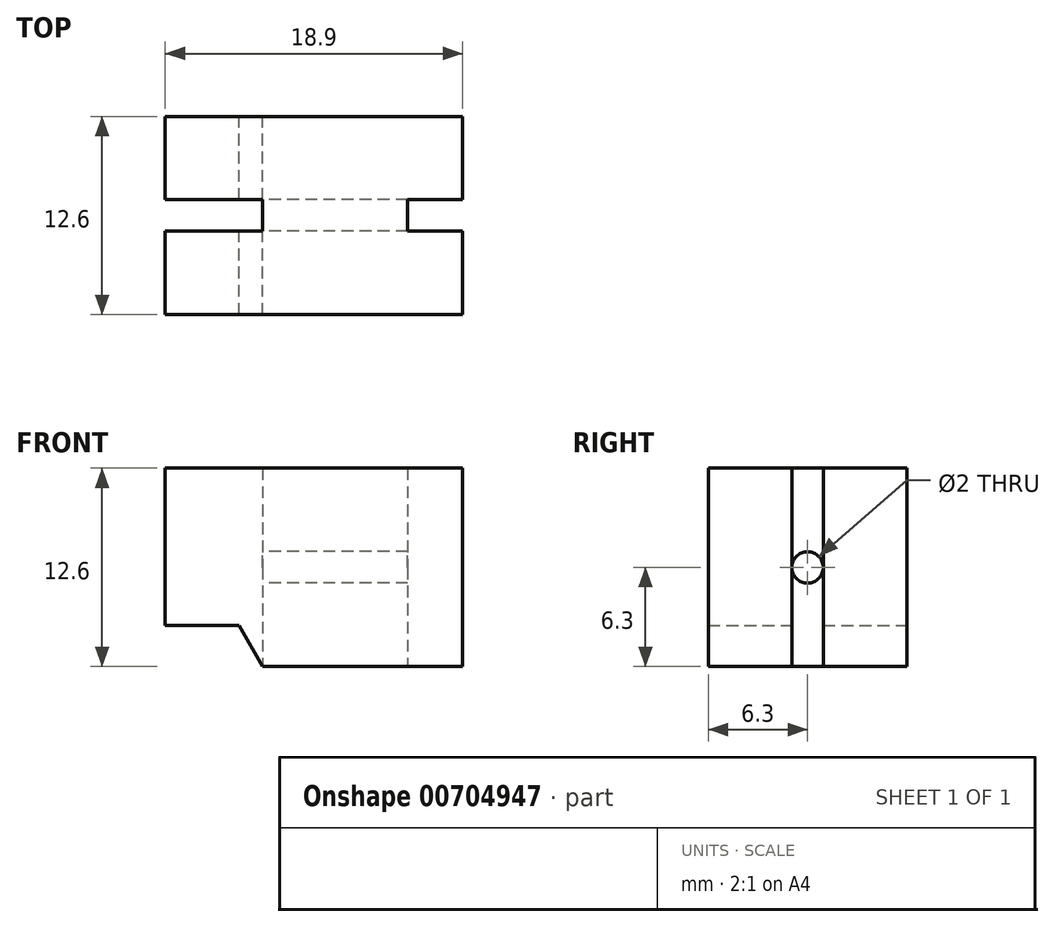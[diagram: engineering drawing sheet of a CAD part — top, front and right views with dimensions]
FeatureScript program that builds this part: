
annotation { "Feature Type Name" : "Feature", "Feature Type Description" : "" }
export const myFeature = defineFeature(function(context is Context, id is Id, definition is map)
    precondition{}
    {
        {
            var Q0;
            Q0=qCreatedBy(makeId("Front.planeOp"),FACE);
            var sketch = newSketch(context, id + "F0", { "sketchPlane" : qUnion([Q0])});
            skLineSegment(sketch, "E0", {"start": v(0, 0) * mm, "end": v(18.9, 0) * mm});
            skLineSegment(sketch, "E1", {"start": v(18.9, 0) * mm, "end": v(18.9, -12.6) * mm});
            skLineSegment(sketch, "E2", {"start": v(18.9, -12.6) * mm, "end": v(6.2, -12.6) * mm});
            skLineSegment(sketch, "E3", {"start": v(6.2, -12.6) * mm, "end": v(0, -12.6) * mm, "construction": true});
            skLineSegment(sketch, "E4", {"start": v(6.2, -12.6) * mm, "end": v(4.7, -10) * mm});
            skLineSegment(sketch, "E5", {"start": v(4.7, -10) * mm, "end": v(0, -10) * mm});
            skLineSegment(sketch, "E6", {"start": v(0, 0) * mm, "end": v(0, -10) * mm});
            skLineSegment(sketch, "E7", {"start": v(0, -12.6) * mm, "end": v(0, -10) * mm, "construction": true});
            skSolve(sketch);
        }
        {
            var Q0;
            Q0=makeQuery(id+"F0.imprint","IMPRINT",FACE,{"disambiguationData":[TD([[makeQuery(id+"F0.imprint","IMPRINT",EDGE,{"derivedFrom":sQuery(id+"F0.wireOp",EDGE,"E0")}),-1.0]])]});
            extrude(context, id + "F1", {"entities" : qUnion([Q0]), "depth" : 12.6 * mm, "offsetDistance" : 25 * mm});
        }
        {
            var Q0;
            Q0=makeQuery(id+"F1.opExtrude","SWEPT_FACE",FACE,{"disambiguationData":[OSD([sQuery(id+"F0.wireOp",EDGE,"E2")])]});
            var sketch = newSketch(context, id + "F2", { "sketchPlane" : qUnion([Q0])});
            skLineSegment(sketch, "E8.bottom", {"start": v(6.2, 7.3) * mm, "end": v(0, 7.3) * mm});
            skLineSegment(sketch, "E8.top", {"start": v(6.2, 5.3) * mm, "end": v(0, 5.3) * mm});
            skLineSegment(sketch, "E8.left", {"start": v(6.2, 7.3) * mm, "end": v(6.2, 5.3) * mm});
            skLineSegment(sketch, "E8.right", {"start": v(0, 7.3) * mm, "end": v(0, 5.3) * mm});
            skPoint(sketch, "E9", {"position": v(6.2, 6.3) * mm});
            skLineSegment(sketch, "E10.bottom", {"start": v(18.9, 7.3) * mm, "end": v(15.4, 7.3) * mm});
            skLineSegment(sketch, "E10.top", {"start": v(18.9, 5.3) * mm, "end": v(15.4, 5.3) * mm});
            skLineSegment(sketch, "E10.left", {"start": v(18.9, 7.3) * mm, "end": v(18.9, 5.3) * mm});
            skLineSegment(sketch, "E10.right", {"start": v(15.4, 7.3) * mm, "end": v(15.4, 5.3) * mm});
            skPoint(sketch, "E10.middle", {"position": v(17.15, 6.3) * mm});
            skPoint(sketch, "E10.middle.positionSnap0", {"position": v(18.9, 6.3) * mm});
            skPoint(sketch, "E10.centerSnap0", {"position": v(18.9, 6.3) * mm});
            skSolve(sketch);
        }
        {
            var Q0;
            Q0=makeQuery(id+"F2.imprint","IMPRINT",FACE,{"disambiguationData":[TD([[makeQuery(id+"F2.imprint","IMPRINT",EDGE,{"derivedFrom":sQuery(id+"F2.wireOp",EDGE,"E8.bottom")}),1.0]])]});
            extrude(context, id + "F3", {"entities" : qUnion([Q0]), "operationType" : NewBodyOperationType.REMOVE, "endBound" : BoundingType.THROUGH_ALL, "oppositeDirection" : true, "depth" : 25 * mm, "offsetDistance" : 25 * mm});
        }
        {
            var Q0;
            Q0=makeQuery(id+"F2.imprint","IMPRINT",FACE,{"disambiguationData":[TD([[makeQuery(id+"F2.imprint","IMPRINT",EDGE,{"derivedFrom":sQuery(id+"F2.wireOp",EDGE,"E10.bottom")}),1.0]])]});
            extrude(context, id + "F4", {"entities" : qUnion([Q0]), "operationType" : NewBodyOperationType.REMOVE, "endBound" : BoundingType.THROUGH_ALL, "oppositeDirection" : true, "depth" : 25 * mm, "offsetDistance" : 25 * mm});
        }
        {
            var Q0;
            Q0=makeQuery(id+"F3.boolean.opBoolean","COPY",FACE,{"derivedFrom":makeQuery(id+"F3.opExtrude","SWEPT_FACE",FACE,{"disambiguationData":[OSD([sQuery(id+"F2.wireOp",EDGE,"E8.left")])]})});
            var sketch = newSketch(context, id + "F5", { "sketchPlane" : qUnion([Q0])});
            skPoint(sketch, "E11", {"position": v(6.3, -6.3) * mm});
            skPoint(sketch, "E11.positionSnap0", {"position": v(6.3, 0) * mm});
            skCircle(sketch, "E12", {"center": v(6.3, -6.3) * mm, "radius": 1 * mm});
            skSolve(sketch);
        }
        {
            var Q0;
            {var subQ0=sQuery(id+"F5.wireOp",EDGE,"E12");var subQ1=sQuery(id+"F2.wireOp",EDGE,"E8.left");var subQ2=sQuery(id+"F0.wireOp",EDGE,"E4");var subQ3=sQuery(id+"F0.wireOp",EDGE,"E2");var subQ4=makeQuery(id+"F5.imprint","INTERSECT",VERTEX,{"derivedFrom":[makeQuery(id+"F3.boolean.opBoolean","COPY",EDGE,{"derivedFrom":makeQuery(id+"F3.opExtrude","SWEPT_EDGE",EDGE,{"disambiguationData":[OSD([subQ3,subQ2,sQuery(id+"F2.wireOp",EDGE,"E8.bottom"),subQ1])]})}),subQ0]});Q0=makeQuery(id+"F5.imprint","IMPRINT",FACE,{"disambiguationData":[TD([[makeQuery(id+"F5.imprint","IMPRINT",EDGE,{"disambiguationData":[TD([[subQ4,-1.0]])],"derivedFrom":subQ0}),1.0]])]});}
            extrude(context, id + "F6", {"entities" : qUnion([Q0]), "operationType" : NewBodyOperationType.REMOVE, "endBound" : BoundingType.THROUGH_ALL, "oppositeDirection" : true, "depth" : 25 * mm, "offsetDistance" : 25 * mm});
        }
    });
